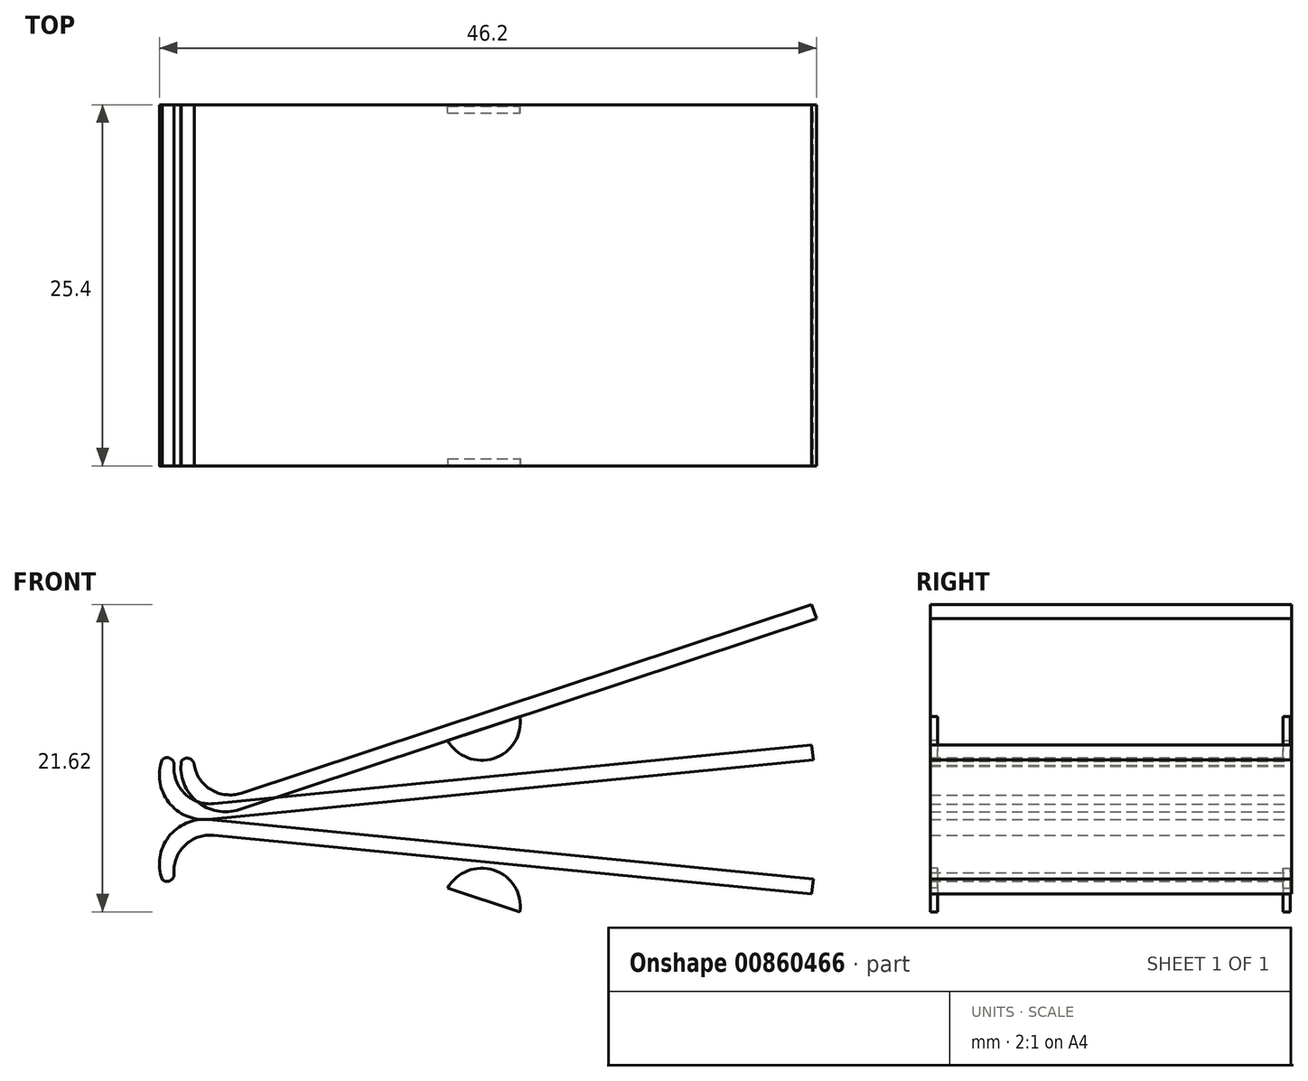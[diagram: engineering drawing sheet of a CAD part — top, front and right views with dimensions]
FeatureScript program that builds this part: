
annotation { "Feature Type Name" : "Feature", "Feature Type Description" : "" }
export const myFeature = defineFeature(function(context is Context, id is Id, definition is map)
    precondition{}
    {
        {
            var Q0;
            Q0=qCreatedBy(makeId("Front.planeOp"),FACE);
            var sketch = newSketch(context, id + "F0", { "sketchPlane" : qUnion([Q0])});
            skLineSegment(sketch, "E0", {"start": v(-38.75, 13.91) * mm, "end": v(-3.03, 37.38) * mm});
            skLineSegment(sketch, "E1", {"start": v(-3.03, 37.38) * mm, "end": v(-3.61, 38.26) * mm});
            skLineSegment(sketch, "E2", {"start": v(-3.61, 38.26) * mm, "end": v(-38.93, 15.06) * mm});
            skArc(sketch, "E3", {"start": v(-42.63, 16.1) * mm, "mid": v(-41.02, 14.74) * mm, "end": v(-38.93, 15.06) * mm});
            skArc(sketch, "E4", {"start": v(-43.57, 16.13) * mm, "mid": v(-41.78, 13.69) * mm, "end": v(-38.75, 13.91) * mm});
            skArc(sketch, "E5", {"start": v(-42.63, 16.1) * mm, "mid": v(-43.09, 16.47) * mm, "end": v(-43.57, 16.13) * mm});
            skSolve(sketch);
        }
        {
            var Q0;
            Q0=makeQuery(id+"F0.imprint","IMPRINT",FACE,{"disambiguationData":[TD([[makeQuery(id+"F0.imprint","IMPRINT",EDGE,{"derivedFrom":sQuery(id+"F0.wireOp",EDGE,"E0")}),1.0]])]});
            extrude(context, id + "F1", {"entities" : qUnion([Q0]), "depth" : 25.4 * mm, "offsetDistance" : 25.4 * mm});
        }
        {
            var Q0;
            Q0=makeQuery(id+"F1.opExtrude","SWEPT_BODY",BODY,{"disambiguationData":[OSD([sQuery(id+"F0.wireOp",EDGE,"3axJKfc3-OAAN-0O4s-hCEc-qYtKJfUsxe7Y"),sQuery(id+"F0.wireOp",EDGE,"MlaEw33F-Ojpc-BA9a-raeR-xKyopvAGnf7Z"),sQuery(id+"F0.wireOp",EDGE,"E0"),sQuery(id+"F0.wireOp",EDGE,"E1"),sQuery(id+"F0.wireOp",EDGE,"E2"),sQuery(id+"F0.wireOp",EDGE,"16ky42as-MlNG-tj4y-t1wu-1ac17YRo9tQa"),sQuery(id+"F0.wireOp",EDGE,"hbJngr0y-QRwY-UoKq-nBPL-aNJjQoa1grGG"),sQuery(id+"F0.wireOp",EDGE,"yBFKE3gm-Mzik-G6mE-UDyS-yzDSILEIpjhQ")])]});
            transform(context, id + "F2", {"entities" : qUnion([Q0]), "transformType" : TransformType.TRANSLATION_3D, "dx" : 0 * mm, "dy" : 0 * mm, "dz" : -12.95 * mm, "makeCopy" : false});
        }
        {
            var Q0;
            Q0=makeQuery(id+"F1.opExtrude","SWEPT_BODY",BODY,{"disambiguationData":[OSD([sQuery(id+"F0.wireOp",EDGE,"3axJKfc3-OAAN-0O4s-hCEc-qYtKJfUsxe7Y"),sQuery(id+"F0.wireOp",EDGE,"MlaEw33F-Ojpc-BA9a-raeR-xKyopvAGnf7Z"),sQuery(id+"F0.wireOp",EDGE,"E0"),sQuery(id+"F0.wireOp",EDGE,"E1"),sQuery(id+"F0.wireOp",EDGE,"E2"),sQuery(id+"F0.wireOp",EDGE,"16ky42as-MlNG-tj4y-t1wu-1ac17YRo9tQa"),sQuery(id+"F0.wireOp",EDGE,"hbJngr0y-QRwY-UoKq-nBPL-aNJjQoa1grGG"),sQuery(id+"F0.wireOp",EDGE,"yBFKE3gm-Mzik-G6mE-UDyS-yzDSILEIpjhQ")])]});
            var Q1;
            Q1=qCreatedBy(makeId("Top.planeOp"),FACE);
            mirror(context, id + "F3", {"entities" : qUnion([Q0]), "mirrorPlane" : qUnion([Q1])});
        }
        {
            var Q0;
            Q0=makeQuery(id+"F1.opExtrude","SWEPT_BODY",BODY,{"disambiguationData":[OSD([sQuery(id+"F0.wireOp",EDGE,"3axJKfc3-OAAN-0O4s-hCEc-qYtKJfUsxe7Y"),sQuery(id+"F0.wireOp",EDGE,"MlaEw33F-Ojpc-BA9a-raeR-xKyopvAGnf7Z"),sQuery(id+"F0.wireOp",EDGE,"E0"),sQuery(id+"F0.wireOp",EDGE,"E1"),sQuery(id+"F0.wireOp",EDGE,"E2"),sQuery(id+"F0.wireOp",EDGE,"16ky42as-MlNG-tj4y-t1wu-1ac17YRo9tQa"),sQuery(id+"F0.wireOp",EDGE,"hbJngr0y-QRwY-UoKq-nBPL-aNJjQoa1grGG"),sQuery(id+"F0.wireOp",EDGE,"yBFKE3gm-Mzik-G6mE-UDyS-yzDSILEIpjhQ")])]});
            var Q1;
            Q1=makeQuery(id+"F1.opExtrude","SWEPT_EDGE",EDGE,{"disambiguationData":[OSD([sQuery(id+"F0.wireOp",EDGE,"E0"),sQuery(id+"F0.wireOp",EDGE,"E1")])]});
            transform(context, id + "F4", {"entities" : qUnion([Q0]), "transformType" : TransformType.ROTATION, "transformAxis" : qUnion([Q1]), "angle" : 15 * degree, "makeCopy" : false});
        }
        {
            var Q0;
            Q0=makeQuery(id+"F3.opPattern","COPY",BODY,{"derivedFrom":makeQuery(id+"F1.opExtrude","SWEPT_BODY",BODY,{"disambiguationData":[OSD([sQuery(id+"F0.wireOp",EDGE,"3axJKfc3-OAAN-0O4s-hCEc-qYtKJfUsxe7Y"),sQuery(id+"F0.wireOp",EDGE,"MlaEw33F-Ojpc-BA9a-raeR-xKyopvAGnf7Z"),sQuery(id+"F0.wireOp",EDGE,"E0"),sQuery(id+"F0.wireOp",EDGE,"E1"),sQuery(id+"F0.wireOp",EDGE,"E2"),sQuery(id+"F0.wireOp",EDGE,"16ky42as-MlNG-tj4y-t1wu-1ac17YRo9tQa"),sQuery(id+"F0.wireOp",EDGE,"hbJngr0y-QRwY-UoKq-nBPL-aNJjQoa1grGG"),sQuery(id+"F0.wireOp",EDGE,"yBFKE3gm-Mzik-G6mE-UDyS-yzDSILEIpjhQ")])]}),"instanceName":"1"});
            deleteBodies(context, id + "F5", {"entities" : qUnion([Q0])});
        }
        {
            var Q0;
            Q0=makeQuery(id+"F1.opExtrude","SWEPT_BODY",BODY,{"disambiguationData":[OSD([sQuery(id+"F0.wireOp",EDGE,"3axJKfc3-OAAN-0O4s-hCEc-qYtKJfUsxe7Y"),sQuery(id+"F0.wireOp",EDGE,"MlaEw33F-Ojpc-BA9a-raeR-xKyopvAGnf7Z"),sQuery(id+"F0.wireOp",EDGE,"E0"),sQuery(id+"F0.wireOp",EDGE,"E1"),sQuery(id+"F0.wireOp",EDGE,"E2"),sQuery(id+"F0.wireOp",EDGE,"16ky42as-MlNG-tj4y-t1wu-1ac17YRo9tQa"),sQuery(id+"F0.wireOp",EDGE,"hbJngr0y-QRwY-UoKq-nBPL-aNJjQoa1grGG"),sQuery(id+"F0.wireOp",EDGE,"yBFKE3gm-Mzik-G6mE-UDyS-yzDSILEIpjhQ")])]});
            transform(context, id + "F6", {"entities" : qUnion([Q0]), "transformType" : TransformType.TRANSLATION_3D, "dx" : 0 * mm, "dy" : 0 * mm, "dz" : -8.38 * mm, "makeCopy" : false});
        }
        {
            var Q0;
            Q0=makeQuery(id+"F1.opExtrude","SWEPT_BODY",BODY,{"disambiguationData":[OSD([sQuery(id+"F0.wireOp",EDGE,"3axJKfc3-OAAN-0O4s-hCEc-qYtKJfUsxe7Y"),sQuery(id+"F0.wireOp",EDGE,"MlaEw33F-Ojpc-BA9a-raeR-xKyopvAGnf7Z"),sQuery(id+"F0.wireOp",EDGE,"E0"),sQuery(id+"F0.wireOp",EDGE,"E1"),sQuery(id+"F0.wireOp",EDGE,"E2"),sQuery(id+"F0.wireOp",EDGE,"16ky42as-MlNG-tj4y-t1wu-1ac17YRo9tQa"),sQuery(id+"F0.wireOp",EDGE,"hbJngr0y-QRwY-UoKq-nBPL-aNJjQoa1grGG"),sQuery(id+"F0.wireOp",EDGE,"yBFKE3gm-Mzik-G6mE-UDyS-yzDSILEIpjhQ")])]});
            var Q1;
            Q1=qCreatedBy(makeId("Top.planeOp"),FACE);
            mirror(context, id + "F7", {"entities" : qUnion([Q0]), "mirrorPlane" : qUnion([Q1])});
        }
        {
            var Q0;
            Q0=makeQuery(id+"F7.opPattern","COPY",BODY,{"derivedFrom":makeQuery(id+"F1.opExtrude","SWEPT_BODY",BODY,{"disambiguationData":[OSD([sQuery(id+"F0.wireOp",EDGE,"E0"),sQuery(id+"F0.wireOp",EDGE,"E1"),sQuery(id+"F0.wireOp",EDGE,"E2"),sQuery(id+"F0.wireOp",EDGE,"E3"),sQuery(id+"F0.wireOp",EDGE,"E4"),sQuery(id+"F0.wireOp",EDGE,"E5")])]}),"instanceName":"1"});
            transform(context, id + "F8", {"entities" : qUnion([Q0]), "transformType" : TransformType.TRANSLATION_3D, "dx" : 0 * mm, "dy" : 0 * mm, "dz" : 4.32 * mm, "makeCopy" : false});
        }
        {
            var Q0;
            Q0=makeQuery(id+"F7.opPattern","COPY",BODY,{"derivedFrom":makeQuery(id+"F1.opExtrude","SWEPT_BODY",BODY,{"disambiguationData":[OSD([sQuery(id+"F0.wireOp",EDGE,"E0"),sQuery(id+"F0.wireOp",EDGE,"E1"),sQuery(id+"F0.wireOp",EDGE,"E2"),sQuery(id+"F0.wireOp",EDGE,"E3"),sQuery(id+"F0.wireOp",EDGE,"E4"),sQuery(id+"F0.wireOp",EDGE,"E5")])]}),"instanceName":"1"});
            deleteBodies(context, id + "F9", {"entities" : qUnion([Q0])});
        }
        {
            var Q0;
            Q0=makeQuery(id+"F1.opExtrude","SWEPT_BODY",BODY,{"disambiguationData":[OSD([sQuery(id+"F0.wireOp",EDGE,"E0"),sQuery(id+"F0.wireOp",EDGE,"E1"),sQuery(id+"F0.wireOp",EDGE,"E2"),sQuery(id+"F0.wireOp",EDGE,"E3"),sQuery(id+"F0.wireOp",EDGE,"E4"),sQuery(id+"F0.wireOp",EDGE,"E5")])]});
            transform(context, id + "F10", {"entities" : qUnion([Q0]), "transformType" : TransformType.TRANSLATION_3D, "dx" : 0 * mm, "dy" : 0 * mm, "dz" : -2.3 * mm, "makeCopy" : false});
        }
        {
            var Q0;
            Q0=makeQuery(id+"F1.opExtrude","CAP_FACE",FACE,{"disambiguationData":[OSD([sQuery(id+"F0.wireOp",EDGE,"E0"),sQuery(id+"F0.wireOp",EDGE,"E1"),sQuery(id+"F0.wireOp",EDGE,"E2"),sQuery(id+"F0.wireOp",EDGE,"E3"),sQuery(id+"F0.wireOp",EDGE,"E4"),sQuery(id+"F0.wireOp",EDGE,"E5")])],"isStart":false});
            var sketch = newSketch(context, id + "F11", { "sketchPlane" : qUnion([Q0])});
            skArc(sketch, "E6", {"start": v(-28.95, 5.19) * mm, "mid": v(-25.72, 3.93) * mm, "end": v(-23.87, 6.86) * mm});
            skSolve(sketch);
        }
        {
            var Q0;
            {var subQ0=sQuery(id+"F11.wireOp",EDGE,"E6");Q0=makeQuery(id+"F11.imprint","IMPRINT",FACE,{"disambiguationData":[TD([[makeQuery(id+"F11.imprint","IMPRINT",EDGE,{"derivedFrom":subQ0}),1.0]])]});}
            extrude(context, id + "F12", {"entities" : qUnion([Q0]), "oppositeDirection" : true, "depth" : 0.5 * mm, "offsetDistance" : 25.4 * mm});
        }
        {
            var Q0;
            Q0=makeQuery(id+"F1.opExtrude","SWEPT_BODY",BODY,{"disambiguationData":[OSD([sQuery(id+"F0.wireOp",EDGE,"E0"),sQuery(id+"F0.wireOp",EDGE,"E1"),sQuery(id+"F0.wireOp",EDGE,"E2"),sQuery(id+"F0.wireOp",EDGE,"E3"),sQuery(id+"F0.wireOp",EDGE,"E4"),sQuery(id+"F0.wireOp",EDGE,"E5")])]});
            var Q1;
            Q1=makeQuery(id+"F12.opExtrude","SWEPT_BODY",BODY,{"disambiguationData":[OSD([sQuery(id+"F0.wireOp",EDGE,"E0"),sQuery(id+"F11.wireOp",EDGE,"E6")])]});
            transform(context, id + "F13", {"entities" : qUnion([Q0, Q1]), "transformType" : TransformType.TRANSLATION_3D, "dx" : 0 * mm, "dy" : 12.5 * mm, "dz" : 0 * mm, "makeCopy" : false});
        }
        {
            var Q0;
            Q0=makeQuery(id+"F12.opExtrude","SWEPT_BODY",BODY,{"disambiguationData":[OSD([sQuery(id+"F0.wireOp",EDGE,"E0"),sQuery(id+"F11.wireOp",EDGE,"E6")])]});
            var Q1;
            Q1=qCreatedBy(makeId("Front.planeOp"),FACE);
            mirror(context, id + "F14", {"entities" : qUnion([Q0]), "mirrorPlane" : qUnion([Q1])});
        }
        {
            var Q0;
            Q0=makeQuery(id+"F14.opPattern","COPY",BODY,{"derivedFrom":makeQuery(id+"F12.opExtrude","SWEPT_BODY",BODY,{"disambiguationData":[OSD([sQuery(id+"F0.wireOp",EDGE,"E0"),sQuery(id+"F11.wireOp",EDGE,"E6")])]}),"instanceName":"1"});
            transform(context, id + "F15", {"entities" : qUnion([Q0]), "transformType" : TransformType.TRANSLATION_3D, "dx" : 0 * mm, "dy" : -0.5 * mm, "dz" : 0 * mm, "makeCopy" : false});
        }
        {
            var Q0;
            Q0=makeQuery(id+"F1.opExtrude","SWEPT_BODY",BODY,{"disambiguationData":[OSD([sQuery(id+"F0.wireOp",EDGE,"E0"),sQuery(id+"F0.wireOp",EDGE,"E1"),sQuery(id+"F0.wireOp",EDGE,"E2"),sQuery(id+"F0.wireOp",EDGE,"E3"),sQuery(id+"F0.wireOp",EDGE,"E4"),sQuery(id+"F0.wireOp",EDGE,"E5")])]});
            var Q1;
            Q1=makeQuery(id+"F12.opExtrude","SWEPT_BODY",BODY,{"disambiguationData":[OSD([sQuery(id+"F0.wireOp",EDGE,"E0"),sQuery(id+"F11.wireOp",EDGE,"E6")])]});
            var Q2;
            Q2=makeQuery(id+"F14.opPattern","COPY",BODY,{"derivedFrom":makeQuery(id+"F12.opExtrude","SWEPT_BODY",BODY,{"disambiguationData":[OSD([sQuery(id+"F0.wireOp",EDGE,"E0"),sQuery(id+"F11.wireOp",EDGE,"E6")])]}),"instanceName":"1"});
            var Q3;
            Q3=qCreatedBy(makeId("Top.planeOp"),FACE);
            mirror(context, id + "F16", {"entities" : qUnion([Q0, Q1, Q2]), "mirrorPlane" : qUnion([Q3])});
        }
        {
            var Q0;
            Q0=makeQuery(id+"F16.opPattern","COPY",BODY,{"derivedFrom":makeQuery(id+"F1.opExtrude","SWEPT_BODY",BODY,{"disambiguationData":[OSD([sQuery(id+"F0.wireOp",EDGE,"E0"),sQuery(id+"F0.wireOp",EDGE,"E1"),sQuery(id+"F0.wireOp",EDGE,"E2"),sQuery(id+"F0.wireOp",EDGE,"E3"),sQuery(id+"F0.wireOp",EDGE,"E4"),sQuery(id+"F0.wireOp",EDGE,"E5")])]}),"instanceName":"1"});
            var Q1;
            Q1=makeQuery(id+"F16.opPattern","COPY",EDGE,{"derivedFrom":makeQuery(id+"F1.opExtrude","SWEPT_EDGE",EDGE,{"disambiguationData":[OSD([sQuery(id+"F0.wireOp",EDGE,"E1"),sQuery(id+"F0.wireOp",EDGE,"E2")])]}),"instanceName":"1"});
            transform(context, id + "F17", {"entities" : qUnion([Q0]), "transformType" : TransformType.ROTATION, "transformAxis" : qUnion([Q1]), "angle" : 12.68 * degree, "oppositeDirection" : true, "makeCopy" : false});
        }
        {
            var Q0;
            Q0=makeQuery(id+"F16.opPattern","COPY",BODY,{"derivedFrom":makeQuery(id+"F1.opExtrude","SWEPT_BODY",BODY,{"disambiguationData":[OSD([sQuery(id+"F0.wireOp",EDGE,"E0"),sQuery(id+"F0.wireOp",EDGE,"E1"),sQuery(id+"F0.wireOp",EDGE,"E2"),sQuery(id+"F0.wireOp",EDGE,"E3"),sQuery(id+"F0.wireOp",EDGE,"E4"),sQuery(id+"F0.wireOp",EDGE,"E5")])]}),"instanceName":"1"});
            transform(context, id + "F18", {"entities" : qUnion([Q0]), "transformType" : TransformType.TRANSLATION_3D, "dx" : 0 * mm, "dy" : 0 * mm, "dz" : 9.14 * mm, "makeCopy" : false});
        }
        {
            var Q0;
            Q0=makeQuery(id+"F16.opPattern","COPY",BODY,{"derivedFrom":makeQuery(id+"F1.opExtrude","SWEPT_BODY",BODY,{"disambiguationData":[OSD([sQuery(id+"F0.wireOp",EDGE,"E0"),sQuery(id+"F0.wireOp",EDGE,"E1"),sQuery(id+"F0.wireOp",EDGE,"E2"),sQuery(id+"F0.wireOp",EDGE,"E3"),sQuery(id+"F0.wireOp",EDGE,"E4"),sQuery(id+"F0.wireOp",EDGE,"E5")])]}),"instanceName":"1"});
            var Q1;
            Q1=qCreatedBy(makeId("Top.planeOp"),FACE);
            mirror(context, id + "F19", {"entities" : qUnion([Q0]), "mirrorPlane" : qUnion([Q1])});
        }
        {
            var Q0;
            Q0=makeQuery(id+"F19.opPattern","COPY",BODY,{"derivedFrom":makeQuery(id+"F16.opPattern","COPY",BODY,{"derivedFrom":makeQuery(id+"F1.opExtrude","SWEPT_BODY",BODY,{"disambiguationData":[OSD([sQuery(id+"F0.wireOp",EDGE,"E0"),sQuery(id+"F0.wireOp",EDGE,"E1"),sQuery(id+"F0.wireOp",EDGE,"E2"),sQuery(id+"F0.wireOp",EDGE,"E3"),sQuery(id+"F0.wireOp",EDGE,"E4"),sQuery(id+"F0.wireOp",EDGE,"E5")])]}),"instanceName":"1"}),"instanceName":"1"});
            transform(context, id + "F20", {"entities" : qUnion([Q0]), "transformType" : TransformType.TRANSLATION_3D, "dx" : 0 * mm, "dy" : 0 * mm, "dz" : -0.74 * mm, "makeCopy" : false});
        }
    });
